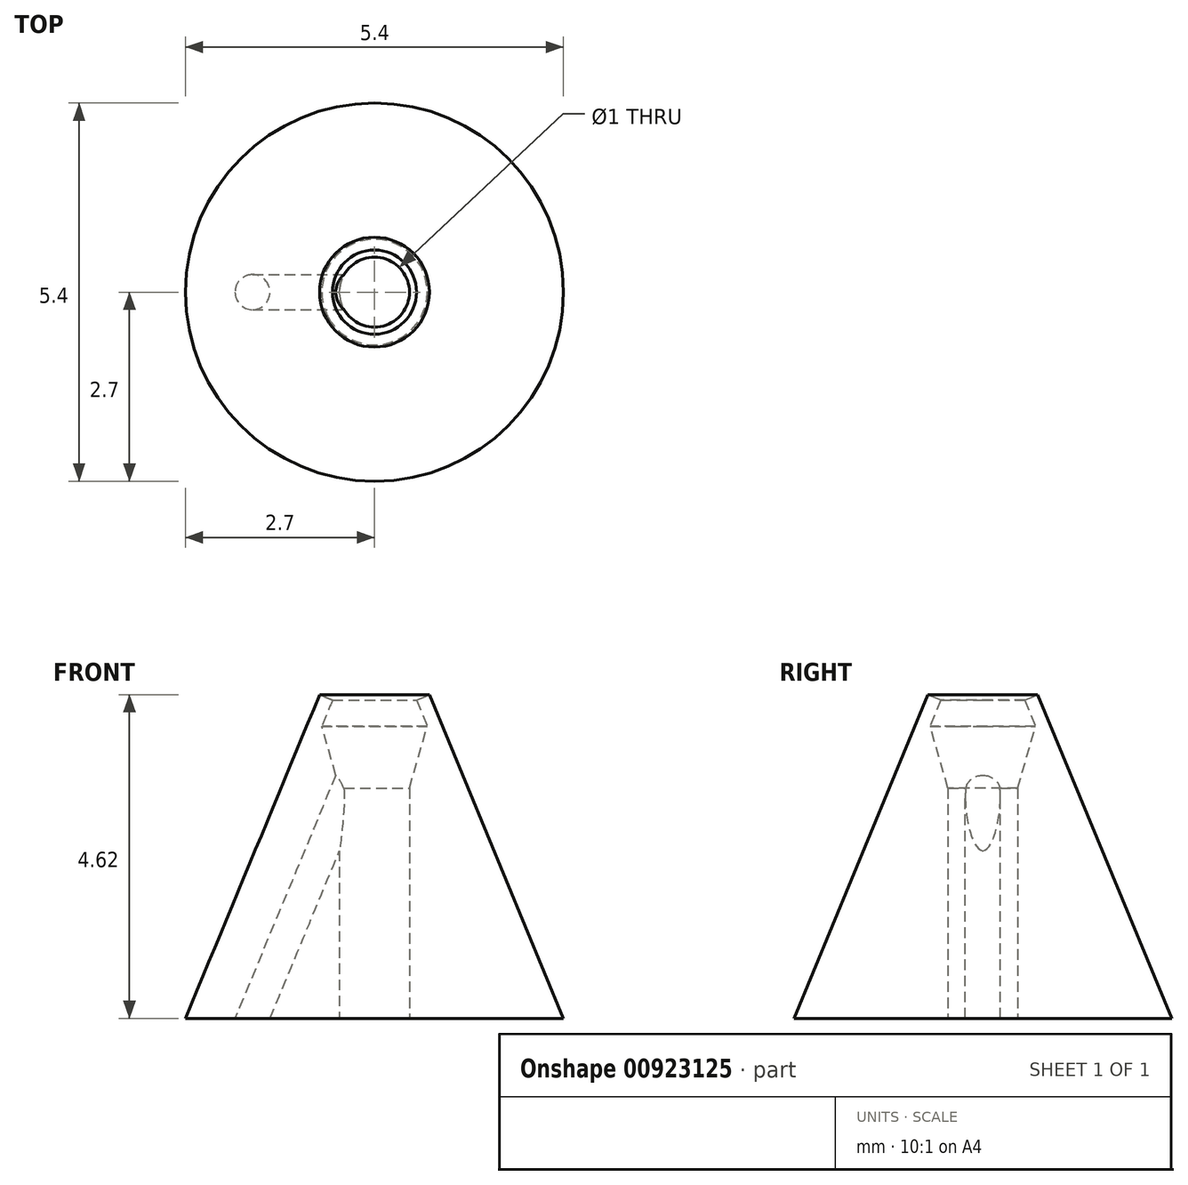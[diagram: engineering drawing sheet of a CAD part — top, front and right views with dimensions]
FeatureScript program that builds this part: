
annotation { "Feature Type Name" : "Feature", "Feature Type Description" : "" }
export const myFeature = defineFeature(function(context is Context, id is Id, definition is map)
    precondition{}
    {
        {
            var Q0;
            Q0=qCreatedBy(makeId("Front.planeOp"),FACE);
            var sketch = newSketch(context, id + "F0", { "sketchPlane" : qUnion([Q0])});
            skLineSegment(sketch, "E0", {"start": v(0, 0) * mm, "end": v(0, 4.17) * mm, "construction": true});
            skLineSegment(sketch, "E1", {"start": v(-0.5, 3.29) * mm, "end": v(-0.5, 0) * mm});
            skLineSegment(sketch, "E2", {"start": v(-0.5, 0) * mm, "end": v(-2.7, 0) * mm});
            skLineSegment(sketch, "E3", {"start": v(0, 0) * mm, "end": v(-0.5, 0) * mm, "construction": true});
            skLineSegment(sketch, "E4", {"start": v(0, 3.29) * mm, "end": v(-0.5, 3.29) * mm, "construction": true});
            skLineSegment(sketch, "E5", {"start": v(-0.75, 4.17) * mm, "end": v(-0.5, 3.29) * mm});
            skLineSegment(sketch, "E6", {"start": v(-0.75, 4.17) * mm, "end": v(-0.6, 4.54) * mm});
            skLineSegment(sketch, "E7", {"start": v(-0.6, 4.54) * mm, "end": v(-0.78, 4.62) * mm});
            skLineSegment(sketch, "E8", {"start": v(-0.78, 4.62) * mm, "end": v(-2.7, 0) * mm});
            skPoint(sketch, "E9.start.orphan", {"position": v(-0.7, 3.29) * mm});
            skLineSegment(sketch, "E10", {"start": v(-0.5, 3.29) * mm, "end": v(-0.5, 5.5) * mm, "construction": true});
            skSolve(sketch);
        }
        {
            var Q0;
            Q0=makeQuery(id+"F0.imprint","IMPRINT",FACE,{"disambiguationData":[TD([[makeQuery(id+"F0.imprint","IMPRINT",EDGE,{"derivedFrom":sQuery(id+"F0.wireOp",EDGE,"E1")}),-1.0]])]});
            var Q1;
            Q1=sQuery(id+"F0.wireOp",EDGE,"E0");
            revolve(context, id + "F1", {"surfaceOperationType" : NewSurfaceOperationType.NEW, "entities" : qUnion([Q0]), "axis" : qUnion([Q1]), "revolveType" : RevolveType.FULL});
        }
        {
            var Q0;
            Q0=qCreatedBy(makeId("Top.planeOp"),FACE);
            cPlane(context, id + "F2", {"entities" : qUnion([Q0]), "cplaneType" : CPlaneType.OFFSET, "offset" : 4.4 * mm, "width" : 150 * mm, "height" : 150 * mm});
        }
        {
            var Q0;
            Q0=makeQuery(id+"F1.opRevolve","SWEPT_FACE",FACE,{"disambiguationData":[OSD([sQuery(id+"F0.wireOp",EDGE,"E2")])]});
            var sketch = newSketch(context, id + "F3", { "sketchPlane" : qUnion([Q0])});
            skCircle(sketch, "E11", {"center": v(-1.74, 0) * mm, "radius": 0.25 * mm});
            skSolve(sketch);
        }
        {
            var Q0;
            Q0=makeQuery(id+"F3.imprint","IMPRINT",FACE,{"disambiguationData":[TD([[makeQuery(id+"F3.imprint","IMPRINT",EDGE,{"derivedFrom":sQuery(id+"F3.wireOp",EDGE,"E11")}),1.0]])]});
            var Q1;
            Q1=sQuery(id+"F0.wireOp",EDGE,"E8");
            sweep(context, id + "F4", {"operationType" : NewBodyOperationType.REMOVE, "profiles" : qUnion([Q0]), "path" : qUnion([Q1])});
        }
    });
